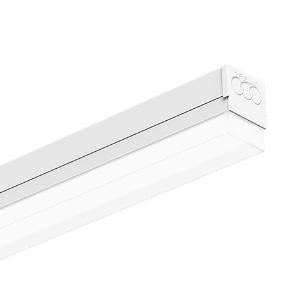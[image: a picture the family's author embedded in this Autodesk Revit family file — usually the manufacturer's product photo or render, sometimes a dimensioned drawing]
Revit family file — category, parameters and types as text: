
# Revit family: 3f_filippi_-_3f_zeta_dr_3f_filippi_-_10970_-_3f_zeta_dr_2x22_led_dali_l1489
name_source: partatom
category: Lighting Fixtures
units: mm (PartAtom-declared; Revit-internal decimal feet)

## family parameters
Cut with Voids When Loaded = No
Host = Face
Light Source = No
Part Type = Normal
Room Calculation Point = No
Round Connector Dimension = Use Diameter
Shared = No

## types (1)
- 3F Filippi - 3F Zeta DR (1 x LED, 6253 lm, 49 W, 4000 K)
    Apparent Load = 49 VA
    Approval mark = CE
    CIE Flux Codes = 41 72 91 86 100
    Color Rendering = 80
    Color Temperature = 4000 K
    Control Gear = Electronic transformer
    Default Elevation = 1800 mm
    Description = ILLUMINOTECHNICAL
Luminous efficiency 100% (DLOR 86%, ULOR 14%).
Initial luminous flux of the luminaire 6253 lm.
Diffused symmetric distribution.
Installation Interdistance Transv.D = 1.31 x hu - Long.D = 1.25 x hu.
Tabular UGR (CIE 117 - 4H-8H; S=0.25H; 70/50/20): RUG 25.7 - 24.2.
Beam angle: 136° - 112°.
Luminous efficacy 128 lm/W.
Lifetime (L93/B10): 30000 h. (tq+25°C)
Lifetime (L90/B10): 50000 h. (tq+25°C)
Lifetime (L85/B10): 80000 h. (tq+25°C)
Lifetime (L80/B10): 100000 h. (tq+25°C)
Sudden decreased luminous flux after 50000 hours: 0% (C0).
Photobiological safety in compliance with IEC/TR 62778: RG0 risk exempt, (IEC 62471).
In compliance with IEC/EN 62722-2-1 - IEC/EN 62717 standards.

SOURCE
2 linear LED modules 22W/840.
Energy efficiency class (UE 2019/2020 - UE 2019/2015): D.
CIE 13.3 Colour rendering index: CRI >80 (R9 <50%).
IES TM-30 Fidelity Index: Rf = 84 Rg = 95.
CCT nominal colour temperature 4000 K.
Colour initial tolerance (MacAdam): SDCM 3.

MECHANICAL
Housing in hot-galvanised steel, painted in white polyester, obtained through rolling process.
Light unit in hot-galvanised steel, painted in white polyester base with fixing springs and retractable safety hooks in stainless steel.
Rectangular screen in self-extinguishing polycarbonate, UV stabilised, opal, with smooth outer surface.
End caps in white polycarbonate.
Pair of stainless steel sliding brackets with sliding block screws.
Luminaire with limited surface temperature. - D - (EN 60598-2-24)
Dimensions: 1489x62 mm, height 81 mm. Weight 3.52 kg.
IP40 protection degree.
Mechanical strength to impacts IK06 (1 joule).
Glow-wire test resistance 850°C.

ELECTRICAL
Halogen Free DALI-2 DATI (Parts 251, 252, 253), PUSH-DIM, electronic wiring 230V-50/60Hz, power factor 0.95 at full load, THD <25%, constant output current, SELV, class I, 1 driver, 1 DALI addresse.
Power of the luminaire 49 W.
ENEC - CE.
SAFE FLICKER: PstLM=<1 and SVM=<0.4 (IEC TR 61547-1 and IEC TR 63158), to ensure a more comfortable and safe light.
Luminaire compliant with EN 60598-2-22 for power supply from a centralised emergency system CPSS (Central Power Supply System), not incorporated in the luminaire - high risk areas excluded. The default power and flux are 100% in AC and 15% in DC.
Ambient temperature from 0°C to +25°C.
Temperature class T6 max 85°C.
Relative humidity UR: <85%.

INSTALLATION
Ceiling / Suspended / Wall.
All accessories dedicated to this product are available on the Catalog and on our website www.3F-Filippi.com.

APPLICATIONS
Suitable product for food production plants (HACCP), IFS (Food Version 6), BRC (GSFS Food Version 7).
In commercial environments, exhibition areas, shops and stores.

LIGHT MANAGEMENT
Recommended minimum setting: 10%.
The luminaire, equipped with (DALI-2 DATI) driver, can be controlled manually with 3F Easy Dim technology or automatically/manually with wired or wireless DALI/D2D control systems.
The D2D driver guarantees interoperability with other devices with the same certification by making the following information available:
Device Data (Part 251), Energy Report (Part 252), Diagnosis & Maintenance (Part 253).
In electrical systems without a regulation system (manual or automatic) and DALI bus, a suitable jumper must be made on the DA-DA terminals of the appliance.

WARNING
Luminaire designed for disposal/recycling at end-of-life.
Replaceable (LED only) light source by a professional. Replaceable control gear by a professional.
    Height = 81 mm
    Lamp = 1 x LED
    Lamp Light Flux = 6253 lm
    Lamp Power = 49 W
    Lamp count = 1
    Length = 1489 mm
    Lifetime = 50000 h
    Luminous efficacy = 128 lm/W
    Manufacturer = 3F Filippi
    ModVariant = No
    Model = 3F Filippi - 10970 - 3F Zeta DR 2x22 LED DALI L1489
    Mounting Place = Ceiling
    Mounting Type = Pendant
    Number of Poles = 1
    OnlyDefault = Yes
    Power Factor = 1
    Product Name = 3F Filippi - 3F Zeta DR
    Product group = pendant luminaire
    ProductGroupID = 9
    Protection Class = Protection class I
    Protection Degree = IP 40
    RLX_Detail_Level = 1
    RLX_Emergency_Light_Flux = 0 lm
    RLX_Emergency_Type = 0
    RLX_Emergency_Type_DB = No
    RlxData = <blob elided: 35321 chars, md5=103d8ea7>
    Socket = socket
    Standby Power = 0 W
    System Light Flux = 6253 lm
    System Power = 49 W
    Type Comments = Product without accessories
    Type Image = 3ffilippi_3f_zeta_dr.jpg
    URL = http://relux.com
    VarID = ---
    Voltage = 0 V
    Weight = 0.00 kg
    Width = 62 mm  [stored 0.203412 ft]

note: [stored X ft] marks values corroborated as IEEE doubles in the binary element streams (Revit-internal decimal feet)

## geometry (parser evidence)
native form markers: Blend x4, Sweep x12
no freeform markers — native parametric forms only
